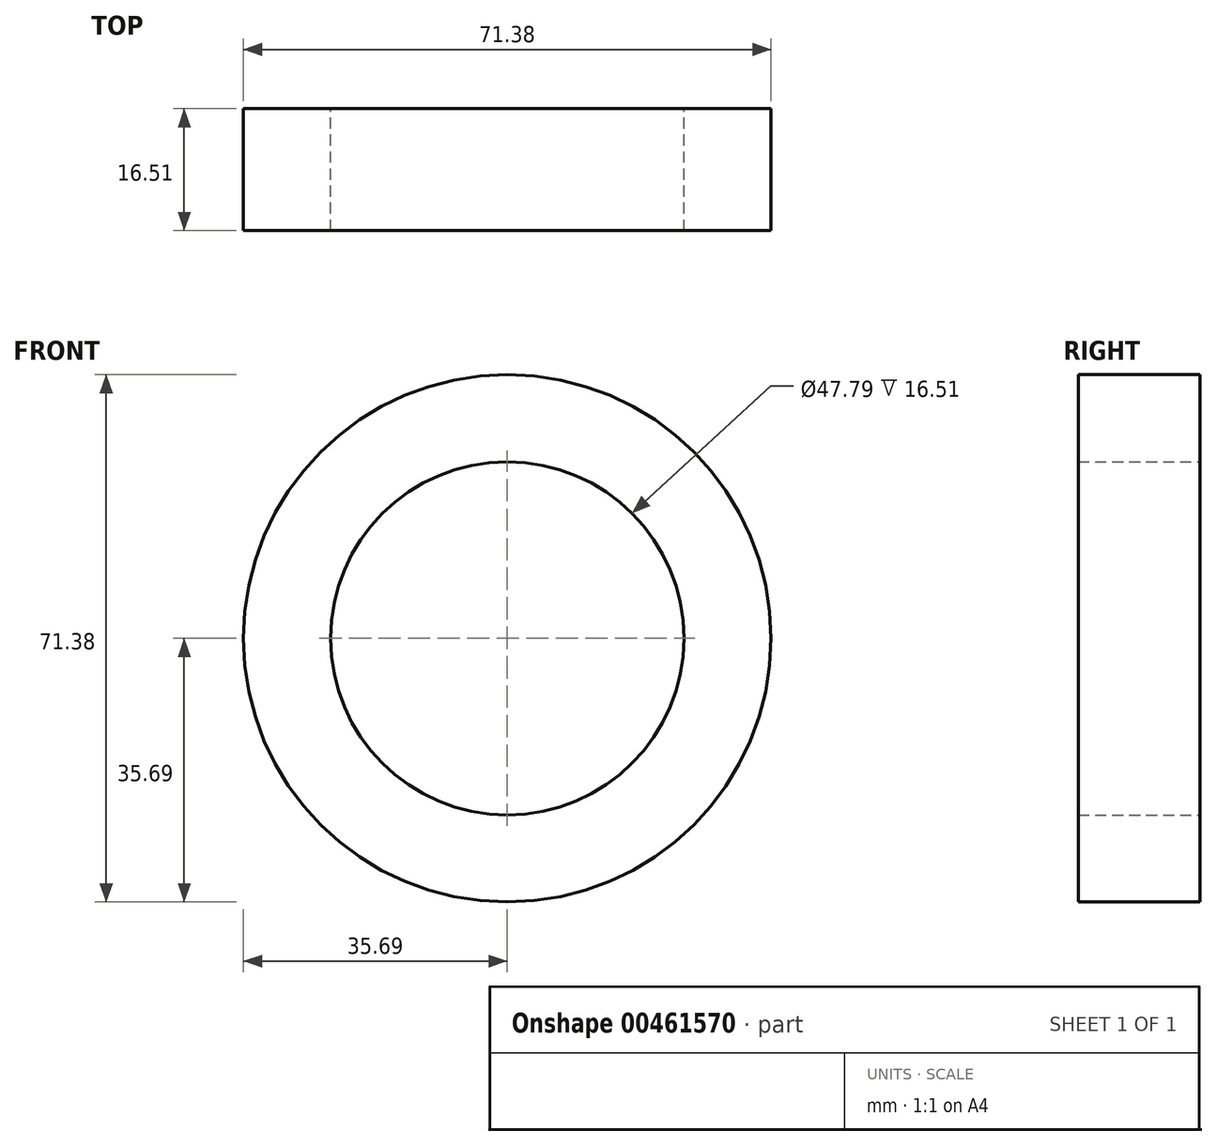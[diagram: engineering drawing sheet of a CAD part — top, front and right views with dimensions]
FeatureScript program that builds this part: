
annotation { "Feature Type Name" : "Feature", "Feature Type Description" : "" }
export const myFeature = defineFeature(function(context is Context, id is Id, definition is map)
    precondition{}
    {
        {
            var Q0;
            Q0=qCreatedBy(makeId("Front.planeOp"),FACE);
            var sketch = newSketch(context, id + "F0", { "sketchPlane" : qUnion([Q0])});
            skCircle(sketch, "E0", {"center": v(0, 0) * mm, "radius": 35.69 * mm});
            skCircle(sketch, "E1", {"center": v(0, 0) * mm, "radius": 23.9 * mm});
            skFitSpline(sketch, "E2", {"points": [v(0, 0) * mm, v(-6.04, 8.06) * mm, v(-6.9, 16.98) * mm, v(-4.48, 23.47) * mm], "startDerivative": vector(-19.88, 20.94) * mm, "endDerivative": vector(9.93, 20.3) * mm});
            skFitSpline(sketch, "E3", {"points": [v(0, 0) * mm, v(6.33, 8.06) * mm, v(6.33, 17.56) * mm, v(4.02, 23.55) * mm], "startDerivative": vector(21.6, 20.36) * mm, "endDerivative": vector(-8.94, 19.02) * mm});
            skFitSpline(sketch, "E4.MirrorCS", {"points": [v(0, 0) * mm, v(6.33, -8.06) * mm, v(6.33, -17.56) * mm, v(4.02, -23.55) * mm], "startDerivative": vector(21.6, -20.36) * mm, "endDerivative": vector(-8.94, -19.02) * mm});
            skFitSpline(sketch, "E5.MirrorCS", {"points": [v(0, 0) * mm, v(-6.04, -8.06) * mm, v(-6.9, -16.98) * mm, v(-4.48, -23.47) * mm], "startDerivative": vector(-19.88, -20.94) * mm, "endDerivative": vector(9.93, -20.3) * mm});
            skFitSpline(sketch, "E6", {"points": [v(0, 0) * mm, v(-9.2, -8.06) * mm, v(-17.84, -8.06) * mm, v(-23.36, -5.03) * mm], "startDerivative": vector(-22.23, -25.72) * mm, "endDerivative": vector(-17.82, 12.33) * mm});
            skFitSpline(sketch, "E7", {"points": [v(-2.4, 2.52) * mm, v(-9.79, 8.06) * mm, v(-16.98, 8.06) * mm, v(-23.26, 5.46) * mm], "startDerivative": vector(-19.5, 18.87) * mm, "endDerivative": vector(-19.29, -9.58) * mm});
            skFitSpline(sketch, "E8.MirrorCS", {"points": [v(0, 0) * mm, v(9.2, -8.06) * mm, v(17.84, -8.06) * mm, v(23.36, -5.03) * mm], "startDerivative": vector(22.23, -25.72) * mm, "endDerivative": vector(17.82, 12.33) * mm});
            skFitSpline(sketch, "E9.MirrorCS", {"points": [v(2.4, 2.52) * mm, v(9.79, 8.06) * mm, v(16.98, 8.06) * mm, v(23.26, 5.46) * mm], "startDerivative": vector(19.5, 18.87) * mm, "endDerivative": vector(19.29, -9.58) * mm});
            skSolve(sketch);
        }
        {
            var Q0;
            Q0=makeQuery(id+"F0.imprint","IMPRINT",FACE,{"disambiguationData":[TD([[makeQuery(id+"F0.imprint","IMPRINT",EDGE,{"derivedFrom":sQuery(id+"F0.wireOp",EDGE,"E0")}),1.0]])]});
            extrude(context, id + "F1", {"entities" : qUnion([Q0]), "depth" : 16.5 * mm});
        }
    });
